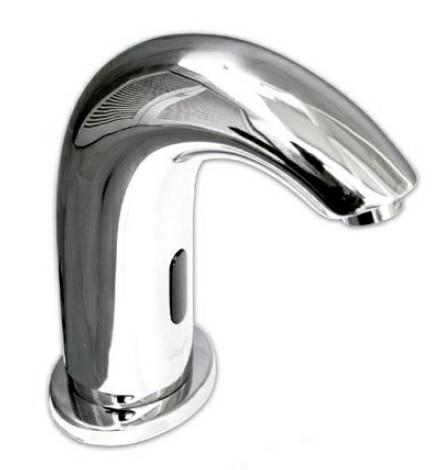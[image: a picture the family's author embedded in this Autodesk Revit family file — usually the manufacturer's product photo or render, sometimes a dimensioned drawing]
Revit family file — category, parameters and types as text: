
# Revit family: HJ2012002
name_source: partatom
category: Plumbing Fixtures
revit_build: Autodesk Revit 2016 (Build: 20150220_1215(x64)
units: mm (PartAtom-declared; Revit-internal decimal feet)

## family parameters
Always vertical = Yes
Cut with Voids When Loaded = No
OmniClass Number = 23.45.00.00
OmniClass Title = Sanitary, Laundry, and Cleaning Equipment
Part Type = Normal
Room Calculation Point = No
Round Connector Dimension = Use Diameter
Shared = No
Work Plane-Based = No

## types (1)
- 160 x 180
    Assembly Code = D2010
    CW Connection = Yes
    Description = Grifería de lavamanos de accionamiento automático. Incorpora un sensor infrarojo de proximidad que la activa cuando el usuario lo requiere. Posee doble opción de suministro eléctrico, por baterías o red 220V. Incorpora una llave de paso mezcladora con filtro que permite la opción de suministrar agua temperada, fria o caliente.
    HW Connection = No
    Height = 800 mm
    Manufacturer = CHC
    Material = Stainless Steel, Polished
    Model = HJ2012002
    Type Image = HJ2012002.jpg
    URL = www.grupochc.cl
    Vent Connection = No
    Waste Connection = No

## geometry (parser evidence)
native form markers: Sweep x3
no freeform markers — native parametric forms only
